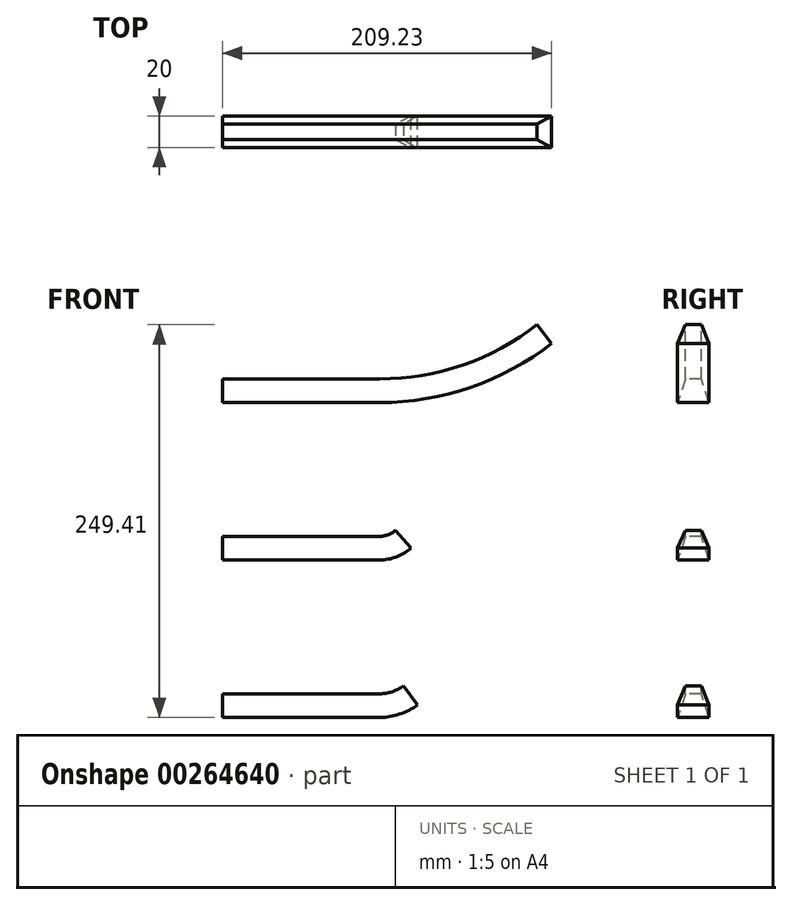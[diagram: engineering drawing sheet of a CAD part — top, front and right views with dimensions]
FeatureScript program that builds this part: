
annotation { "Feature Type Name" : "Feature", "Feature Type Description" : "" }
export const myFeature = defineFeature(function(context is Context, id is Id, definition is map)
    precondition{}
    {
        {
            var Q0;
            Q0=qCreatedBy(makeId("Front.planeOp"),FACE);
            var sketch = newSketch(context, id + "F0", { "sketchPlane" : qUnion([Q0])});
            skLineSegment(sketch, "E0", {"start": v(0, 0) * mm, "end": v(100, 0) * mm});
            skArc(sketch, "E1", {"start": v(100, 0) * mm, "mid": v(152.88, 8.84) * mm, "end": v(200, 34.41) * mm});
            skLineSegment(sketch, "E2", {"start": v(0, -200) * mm, "end": v(100, -200) * mm});
            skArc(sketch, "E3", {"start": v(100, -200) * mm, "mid": v(107.9, -198.72) * mm, "end": v(115, -195) * mm});
            skLineSegment(sketch, "E4", {"start": v(0, -100) * mm, "end": v(100, -100) * mm});
            skArc(sketch, "E5", {"start": v(100, -100) * mm, "mid": v(105.35, -99.01) * mm, "end": v(110, -96.18) * mm});
            skSolve(sketch);
        }
        {
            var Q0;
            Q0=qCreatedBy(makeId("Right.planeOp"),FACE);
            var sketch = newSketch(context, id + "F1", { "sketchPlane" : qUnion([Q0])});
            skLineSegment(sketch, "E6", {"start": v(0, 0) * mm, "end": v(0, -100) * mm});
            skLineSegment(sketch, "E7", {"start": v(0, -100) * mm, "end": v(0, -200) * mm});
            skLineSegment(sketch, "E8", {"start": v(0, 0) * mm, "end": v(-5, 0) * mm});
            skLineSegment(sketch, "E9", {"start": v(-5, 0) * mm, "end": v(-10, -15) * mm});
            skLineSegment(sketch, "E10", {"start": v(-10, -15) * mm, "end": v(10, -15) * mm});
            skLineSegment(sketch, "E11", {"start": v(10, -15) * mm, "end": v(5, 0) * mm});
            skLineSegment(sketch, "E12", {"start": v(5, 0) * mm, "end": v(0, 0) * mm});
            skLineSegment(sketch, "E13", {"start": v(0, -100) * mm, "end": v(-5, -100) * mm});
            skLineSegment(sketch, "E14", {"start": v(-5, -100) * mm, "end": v(-10, -115) * mm});
            skLineSegment(sketch, "E15", {"start": v(-10, -115) * mm, "end": v(10, -115) * mm});
            skLineSegment(sketch, "E16", {"start": v(10, -115) * mm, "end": v(5, -100) * mm});
            skLineSegment(sketch, "E17", {"start": v(5, -100) * mm, "end": v(0, -100) * mm});
            skLineSegment(sketch, "E18", {"start": v(0, -200) * mm, "end": v(-5, -200) * mm});
            skLineSegment(sketch, "E19", {"start": v(-5, -200) * mm, "end": v(-10, -215) * mm});
            skLineSegment(sketch, "E20", {"start": v(-10, -215) * mm, "end": v(10, -215) * mm});
            skLineSegment(sketch, "E21", {"start": v(10, -215) * mm, "end": v(5, -200) * mm});
            skLineSegment(sketch, "E22", {"start": v(5, -200) * mm, "end": v(0, -200) * mm});
            skSolve(sketch);
        }
        {
            var Q0;
            Q0=makeQuery(id+"F1.imprint","IMPRINT",FACE,{"disambiguationData":[TD([[makeQuery(id+"F1.imprint","IMPRINT",EDGE,{"derivedFrom":sQuery(id+"F1.wireOp",EDGE,"E18")}),1.0]])]});
            var Q1;
            Q1=sQuery(id+"F0.wireOp",EDGE,"E2");
            var Q2;
            Q2=sQuery(id+"F0.wireOp",EDGE,"E3");
            sweep(context, id + "F2", {"profiles" : qUnion([Q0]), "path" : qUnion([Q1, Q2])});
        }
        {
            var Q0;
            {var subQ4=sQuery(id+"F1.wireOp",EDGE,"E16");Q0=makeQuery(id+"F1.imprint","IMPRINT",FACE,{"disambiguationData":[TD([[makeQuery(id+"F1.imprint","IMPRINT",EDGE,{"derivedFrom":subQ4}),1.0]])]});}
            var Q1;
            {var subQ0=sQuery(id+"F1.wireOp",EDGE,"E13");Q1=makeQuery(id+"F1.imprint","IMPRINT",FACE,{"disambiguationData":[TD([[makeQuery(id+"F1.imprint","IMPRINT",EDGE,{"derivedFrom":subQ0}),1.0]])]});}
            var Q2;
            Q2=sQuery(id+"F0.wireOp",EDGE,"E4");
            var Q3;
            Q3=sQuery(id+"F0.wireOp",EDGE,"E5");
            sweep(context, id + "F3", {"profiles" : qUnion([Q0, Q1]), "path" : qUnion([Q2, Q3])});
        }
        {
            var Q0;
            {var subQ0=sQuery(id+"F1.wireOp",EDGE,"E8");Q0=makeQuery(id+"F1.imprint","IMPRINT",FACE,{"disambiguationData":[TD([[makeQuery(id+"F1.imprint","IMPRINT",EDGE,{"derivedFrom":subQ0}),1.0]])]});}
            var Q1;
            {var subQ4=sQuery(id+"F1.wireOp",EDGE,"E11");Q1=makeQuery(id+"F1.imprint","IMPRINT",FACE,{"disambiguationData":[TD([[makeQuery(id+"F1.imprint","IMPRINT",EDGE,{"derivedFrom":subQ4}),1.0]])]});}
            var Q2;
            Q2=sQuery(id+"F0.wireOp",EDGE,"E0");
            var Q3;
            Q3=sQuery(id+"F0.wireOp",EDGE,"E1");
            sweep(context, id + "F4", {"profiles" : qUnion([Q0, Q1]), "path" : qUnion([Q2, Q3])});
        }
    });
